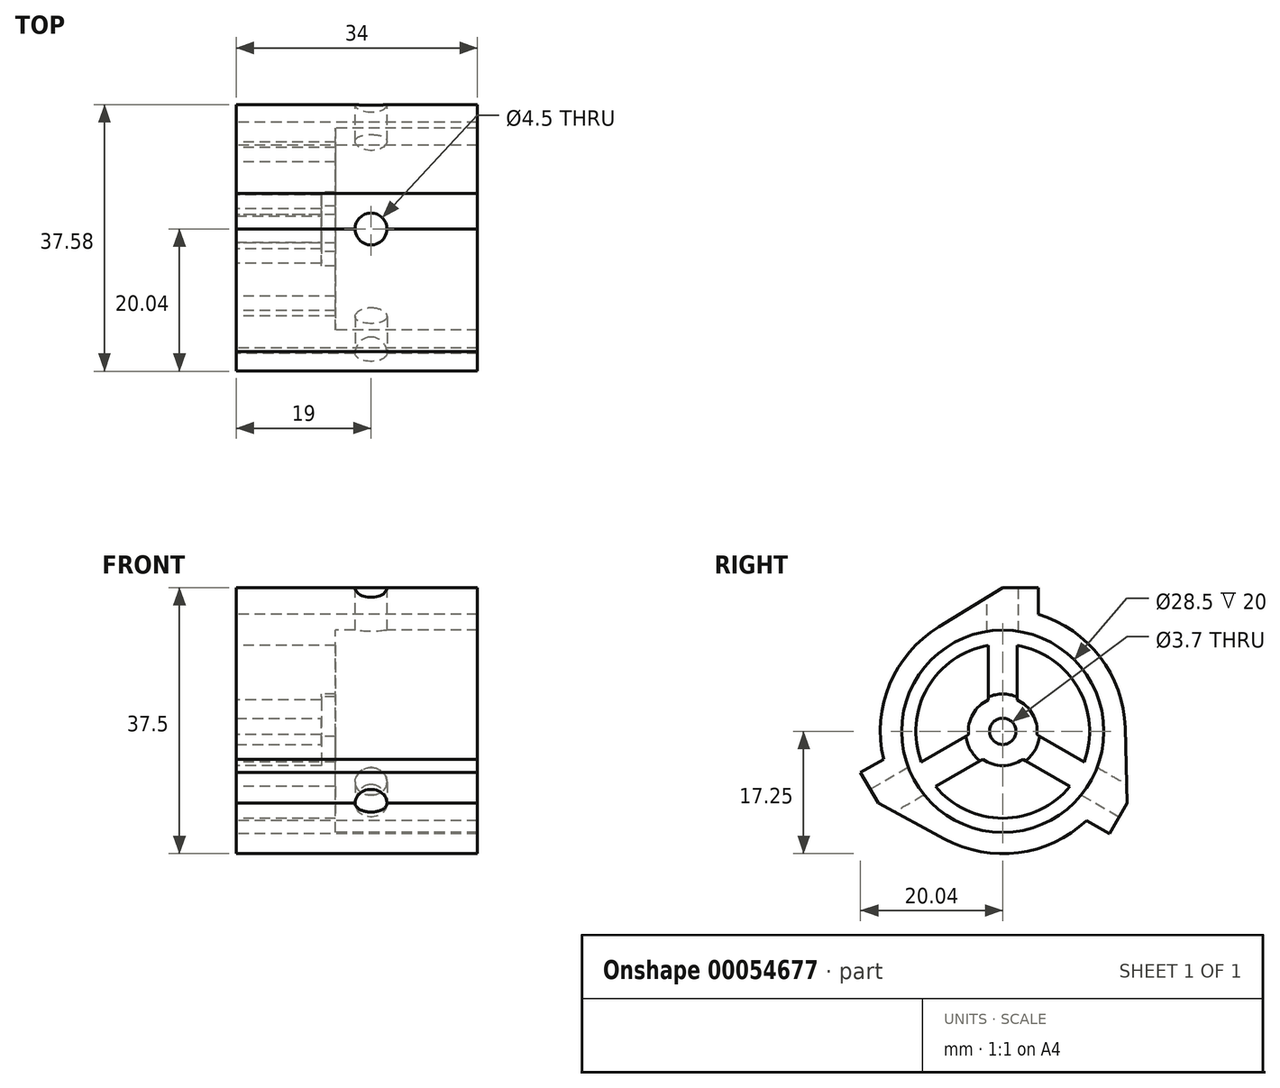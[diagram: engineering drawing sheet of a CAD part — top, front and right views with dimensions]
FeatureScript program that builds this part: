
annotation { "Feature Type Name" : "Feature", "Feature Type Description" : "" }
export const myFeature = defineFeature(function(context is Context, id is Id, definition is map)
    precondition{}
    {
        {
            var Q0;
            Q0=qCreatedBy(makeId("Right.planeOp"),FACE);
            var sketch = newSketch(context, id + "F0", { "sketchPlane" : qUnion([Q0])});
            skCircle(sketch, "E0", {"center": v(0, 0) * mm, "radius": 5.25 * mm});
            skCircle(sketch, "E1", {"center": v(0, 0) * mm, "radius": 1.85 * mm});
            skCircle(sketch, "E2", {"center": v(0, 0) * mm, "radius": 14.25 * mm});
            skCircle(sketch, "E3", {"center": v(0, 0) * mm, "radius": 17.25 * mm});
            skSolve(sketch);
        }
        {
            var Q0;
            Q0 = qSketchRegion(id + "F0", true);
            extrude(context, id + "F1", {"entities" : qUnion([Q0]), "depth" : 22 * mm});
        }
        {
            var Q0;
            Q0 = qSketchRegion(id + "F0", true);
            var Q1;
            Q1=makeQuery(id+"F0.imprint","IMPRINT",FACE,{"disambiguationData":[TD([[makeQuery(id+"F0.imprint","IMPRINT",EDGE,{"derivedFrom":sQuery(id+"F0.wireOp",EDGE,"E0")}),-1.0]])]});
            extrude(context, id + "F2", {"entities" : qUnion([Q0, Q1]), "operationType" : NewBodyOperationType.ADD, "depth" : 2 * mm});
        }
        {
            var Q0;
            Q0=makeQuery(id+"F0.imprint","IMPRINT",FACE,{"disambiguationData":[TD([[makeQuery(id+"F0.imprint","IMPRINT",EDGE,{"derivedFrom":sQuery(id+"F0.wireOp",EDGE,"E2")}),-1.0]])]});
            var Q1;
            Q1=makeQuery(id+"F0.imprint","IMPRINT",FACE,{"disambiguationData":[TD([[makeQuery(id+"F0.imprint","IMPRINT",EDGE,{"derivedFrom":sQuery(id+"F0.wireOp",EDGE,"E0")}),-1.0]])]});
            var Q2;
            Q2=makeQuery(id+"F0.imprint","IMPRINT",FACE,{"disambiguationData":[TD([[makeQuery(id+"F0.imprint","IMPRINT",EDGE,{"derivedFrom":sQuery(id+"F0.wireOp",EDGE,"E0")}),1.0]])]});
            extrude(context, id + "F3", {"entities" : qUnion([Q0, Q1, Q2]), "operationType" : NewBodyOperationType.ADD, "oppositeDirection" : true, "depth" : 12 * mm});
        }
        {
            var Q0;
            Q0=makeQuery(id+"F3.opExtrude","CAP_FACE",FACE,{"disambiguationData":[OSD([sQuery(id+"F0.wireOp",EDGE,"E1"),sQuery(id+"F0.wireOp",EDGE,"E3")])],"isStart":false});
            var sketch = newSketch(context, id + "F4", { "sketchPlane" : qUnion([Q0])});
            skLineSegment(sketch, "E4", {"start": v(0, 31.55) * mm, "end": v(0, -29.15) * mm, "construction": true});
            skLineSegment(sketch, "E5", {"start": v(-5, 16.5) * mm, "end": v(-5, 20.25) * mm});
            skLineSegment(sketch, "E6", {"start": v(-5, 20.25) * mm, "end": v(0, 20.25) * mm});
            skLineSegment(sketch, "E7", {"start": v(0, 20.25) * mm, "end": v(9.04, 14.7) * mm});
            skArc(sketch, "E8", {"start": v(-5, 16.5) * mm, "mid": v(2.21, 17.1) * mm, "end": v(9.04, 14.7) * mm});
            skLineSegment(sketch, "E9", {"start": v(17.25, 0) * mm, "end": v(-17.25, 0) * mm, "construction": true});
            skLineSegment(sketch, "E10.1.0", {"start": v(-11.8, -12.58) * mm, "end": v(-15.04, -14.46) * mm});
            skLineSegment(sketch, "E10.1.1", {"start": v(-15.04, -14.46) * mm, "end": v(-17.54, -10.12) * mm});
            skArc(sketch, "E10.1.2", {"start": v(-11.8, -12.58) * mm, "mid": v(-15.92, -6.64) * mm, "end": v(-17.24, 0.48) * mm});
            skLineSegment(sketch, "E10.1.3", {"start": v(-17.54, -10.12) * mm, "end": v(-17.24, 0.48) * mm});
            skLineSegment(sketch, "E10.2.0", {"start": v(16.8, -3.92) * mm, "end": v(20.04, -5.8) * mm});
            skLineSegment(sketch, "E10.2.1", {"start": v(20.04, -5.8) * mm, "end": v(17.54, -10.13) * mm});
            skArc(sketch, "E10.2.2", {"start": v(16.8, -3.92) * mm, "mid": v(13.7, -10.47) * mm, "end": v(8.2, -15.17) * mm});
            skLineSegment(sketch, "E10.2.3", {"start": v(17.54, -10.13) * mm, "end": v(8.2, -15.17) * mm});
            skSolve(sketch);
        }
        {
            var Q0;
            Q0 = qSketchRegion(id + "F4", true);
            var Q1;
            Q1=makeQuery(id+"F1.opExtrude","CAP_FACE",FACE,{"disambiguationData":[OSD([sQuery(id+"F0.wireOp",EDGE,"E2"),sQuery(id+"F0.wireOp",EDGE,"E3")])],"isStart":false});
            extrude(context, id + "F5", {"entities" : qUnion([Q0]), "operationType" : NewBodyOperationType.ADD, "endBound" : BoundingType.UP_TO_SURFACE, "oppositeDirection" : true, "endBoundEntityFace" : qUnion([Q1]), "depth" : 25 * mm});
        }
        {
            var Q0;
            Q0=makeQuery(id+"F5.opExtrude","SWEPT_FACE",FACE,{"disambiguationData":[OSD([sQuery(id+"F4.wireOp",EDGE,"E6")])]});
            var sketch = newSketch(context, id + "F6", { "sketchPlane" : qUnion([Q0])});
            skCircle(sketch, "E11", {"center": v(7, 0) * mm, "radius": 2.25 * mm});
            skSolve(sketch);
        }
        {
            var Q0;
            {var subQ0=sQuery(id+"F6.wireOp",EDGE,"E11");var subQ1=makeQuery(id+"F5.opExtrude","SWEPT_EDGE",EDGE,{"disambiguationData":[OSD([sQuery(id+"F4.wireOp",EDGE,"E6"),sQuery(id+"F4.wireOp",EDGE,"E7")])]});var subQ2=makeQuery(id+"F6.imprint","INTERSECT",VERTEX,{"disambiguationData":[OD(0.0)],"derivedFrom":[subQ1,subQ0]});Q0=makeQuery(id+"F6.imprint","IMPRINT",FACE,{"disambiguationData":[TD([[makeQuery(id+"F6.imprint","IMPRINT",EDGE,{"disambiguationData":[TD([[subQ2,-1.0]])],"derivedFrom":subQ0}),1.0]])]});}
            var Q1;
            {var subQ0=sQuery(id+"F6.wireOp",EDGE,"E11");var subQ1=makeQuery(id+"F5.opExtrude","SWEPT_EDGE",EDGE,{"disambiguationData":[OSD([sQuery(id+"F4.wireOp",EDGE,"E6"),sQuery(id+"F4.wireOp",EDGE,"E7")])]});var subQ2=makeQuery(id+"F6.imprint","INTERSECT",VERTEX,{"disambiguationData":[OD(0.0)],"derivedFrom":[subQ1,subQ0]});Q1=makeQuery(id+"F6.imprint","IMPRINT",FACE,{"disambiguationData":[TD([[makeQuery(id+"F6.imprint","IMPRINT",EDGE,{"disambiguationData":[TD([[subQ2,1.0]])],"derivedFrom":subQ0}),1.0]])]});}
            var Q2;
            Q2=makeQuery(id+"F1.opExtrude","SWEPT_FACE",FACE,{"disambiguationData":[OSD([sQuery(id+"F0.wireOp",EDGE,"E2")])]});
            extrude(context, id + "F7", {"entities" : qUnion([Q0, Q1]), "operationType" : NewBodyOperationType.REMOVE, "endBound" : BoundingType.UP_TO_SURFACE, "oppositeDirection" : true, "endBoundEntityFace" : qUnion([Q2]), "depth" : 25 * mm});
        }
        {
            var Q0;
            Q0=makeQuery(id+"F5.opExtrude","SWEPT_FACE",FACE,{"disambiguationData":[OSD([sQuery(id+"F4.wireOp",EDGE,"E10.1.1")])]});
            var sketch = newSketch(context, id + "F8", { "sketchPlane" : qUnion([Q0])});
            skCircle(sketch, "E12", {"center": v(-7, 0) * mm, "radius": 2.25 * mm});
            skSolve(sketch);
        }
        {
            var Q0;
            Q0=makeQuery(id+"F5.opExtrude","SWEPT_FACE",FACE,{"disambiguationData":[OSD([sQuery(id+"F4.wireOp",EDGE,"E10.2.1")])]});
            var sketch = newSketch(context, id + "F9", { "sketchPlane" : qUnion([Q0])});
            skCircle(sketch, "E13", {"center": v(7, 0) * mm, "radius": 2.25 * mm});
            skSolve(sketch);
        }
        {
            var Q0;
            Q0 = qSketchRegion(id + "F8", true);
            var Q1;
            Q1=makeQuery(id+"F1.opExtrude","SWEPT_FACE",FACE,{"disambiguationData":[OSD([sQuery(id+"F0.wireOp",EDGE,"E2")])]});
            extrude(context, id + "F10", {"entities" : qUnion([Q0]), "operationType" : NewBodyOperationType.REMOVE, "endBound" : BoundingType.UP_TO_SURFACE, "oppositeDirection" : true, "endBoundEntityFace" : qUnion([Q1]), "depth" : 25 * mm});
        }
        {
            var Q0;
            Q0 = qSketchRegion(id + "F9", true);
            var Q1;
            Q1=makeQuery(id+"F1.opExtrude","SWEPT_FACE",FACE,{"disambiguationData":[OSD([sQuery(id+"F0.wireOp",EDGE,"E2")])]});
            extrude(context, id + "F11", {"entities" : qUnion([Q0]), "operationType" : NewBodyOperationType.REMOVE, "endBound" : BoundingType.UP_TO_SURFACE, "oppositeDirection" : true, "endBoundEntityFace" : qUnion([Q1]), "depth" : 25 * mm});
        }
        {
            var Q0;
            Q0=makeQuery(id+"F5.boolean.opBoolean","MERGE",FACE,{"derivedFrom":[makeQuery(id+"F3.opExtrude","CAP_FACE",FACE,{"disambiguationData":[OSD([sQuery(id+"F0.wireOp",EDGE,"E1"),sQuery(id+"F0.wireOp",EDGE,"E3")])],"isStart":false}),makeQuery(id+"F5.opExtrude","CAP_FACE",FACE,{"disambiguationData":[OSD([sQuery(id+"F4.wireOp",EDGE,"E5"),sQuery(id+"F4.wireOp",EDGE,"E6"),sQuery(id+"F4.wireOp",EDGE,"E7"),sQuery(id+"F4.wireOp",EDGE,"E8")])],"isStart":true}),makeQuery(id+"F5.opExtrude","CAP_FACE",FACE,{"disambiguationData":[OSD([sQuery(id+"F4.wireOp",EDGE,"E10.1.0"),sQuery(id+"F4.wireOp",EDGE,"E10.1.1"),sQuery(id+"F4.wireOp",EDGE,"E10.1.2"),sQuery(id+"F4.wireOp",EDGE,"E10.1.3")])],"isStart":true}),makeQuery(id+"F5.opExtrude","CAP_FACE",FACE,{"disambiguationData":[OSD([sQuery(id+"F4.wireOp",EDGE,"E10.2.0"),sQuery(id+"F4.wireOp",EDGE,"E10.2.1"),sQuery(id+"F4.wireOp",EDGE,"E10.2.2"),sQuery(id+"F4.wireOp",EDGE,"E10.2.3")])],"isStart":true})]});
            var sketch = newSketch(context, id + "F12", { "sketchPlane" : qUnion([Q0])});
            skCircle(sketch, "E14", {"center": v(0, 0) * mm, "radius": 17.25 * mm});
            skCircle(sketch, "E15", {"center": v(0, 0) * mm, "radius": 4.85 * mm});
            skCircle(sketch, "E16", {"center": v(0, 0) * mm, "radius": 12.25 * mm});
            skLineSegment(sketch, "E17", {"start": v(0, 4.85) * mm, "end": v(0, 12.25) * mm, "construction": true});
            skLineSegment(sketch, "E18", {"start": v(-2, 4.42) * mm, "end": v(-2, 12.09) * mm});
            skLineSegment(sketch, "E19.MirrorCS", {"start": v(2, 4.42) * mm, "end": v(2, 12.09) * mm});
            skLineSegment(sketch, "E20.1.0", {"start": v(-2.83, -3.94) * mm, "end": v(-9.47, -7.77) * mm});
            skLineSegment(sketch, "E20.1.1", {"start": v(-4.83, -0.48) * mm, "end": v(-11.47, -4.31) * mm});
            skLineSegment(sketch, "E20.2.0", {"start": v(4.83, -0.48) * mm, "end": v(11.47, -4.31) * mm});
            skLineSegment(sketch, "E20.2.1", {"start": v(2.83, -3.94) * mm, "end": v(9.47, -7.77) * mm});
            skSolve(sketch);
        }
        {
            var Q0;
            {var subQ0=sQuery(id+"F12.wireOp",EDGE,"E18");Q0=makeQuery(id+"F12.imprint","IMPRINT",FACE,{"disambiguationData":[TD([[makeQuery(id+"F12.imprint","IMPRINT",EDGE,{"derivedFrom":subQ0}),1.0]])]});}
            var Q1;
            {var subQ0=sQuery(id+"F12.wireOp",EDGE,"E19.MirrorCS");Q1=makeQuery(id+"F12.imprint","IMPRINT",FACE,{"disambiguationData":[TD([[makeQuery(id+"F12.imprint","IMPRINT",EDGE,{"derivedFrom":subQ0}),-1.0]])]});}
            var Q2;
            {var subQ0=sQuery(id+"F12.wireOp",EDGE,"E20.1.0");Q2=makeQuery(id+"F12.imprint","IMPRINT",FACE,{"disambiguationData":[TD([[makeQuery(id+"F12.imprint","IMPRINT",EDGE,{"derivedFrom":subQ0}),1.0]])]});}
            extrude(context, id + "F13", {"entities" : qUnion([Q0, Q1, Q2]), "operationType" : NewBodyOperationType.REMOVE, "oppositeDirection" : true, "depth" : 25 * mm});
        }
    });
